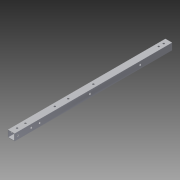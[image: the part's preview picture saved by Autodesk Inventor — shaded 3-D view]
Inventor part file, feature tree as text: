
AUTODESK INVENTOR PART (.ipt)
format: ipt  version: 2014 SP1 (Build 180222100, 222)  size: 117,760 bytes
history: native  units: in
note: dims shown in document units (in); Inventor stores cm internally (conversion verified against a paired STEP export)
features: reference x8, extrude x3, sketch x3
ambient origin geometry x8: Origin, YZ Plane, XZ Plane, XY Plane, X Axis, Y Axis, Z Axis, Center Point
bodies: Solid1 (feature_tree)
feature tree (14):
  extrude  "Extrusion1"  Depth=1.0in
  extrude  "Extrusion3"  Depth=23.5in TaperAngle=0.0deg
  extrude  "Extrusion4"  Depth=1.0in TaperAngle=0.0deg
  sketch  "Sketch1"  dims[d0=1.0in d2=1.0in]
  sketch  "Sketch3"  dims[d3=0.0625in d4=23.5in d5=0.0in]
  reference  "Reference3"
  reference  "Reference4"
  sketch  "Sketch4"  dims[d8=1.0in d9=0.0in d10=1.0in d11=0.0in d12=1.25in d13=1.1811in d15=7.5in d16=0.3937in d18=1.0in]
  reference  "Reference5"
  reference  "Reference6"
  reference  "Reference7"
  reference  "Reference8"
  reference  "Reference9"
  reference  "Reference11"
